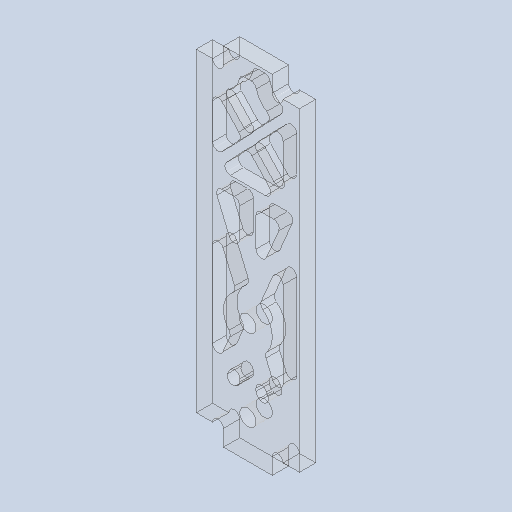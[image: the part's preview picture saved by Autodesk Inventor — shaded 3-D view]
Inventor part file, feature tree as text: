
AUTODESK INVENTOR PART (.ipt)
format: ipt  version: 2023 (Build 270158030, 158C)  size: 849,408 bytes
history: native  units: mm
features: sketch x19, other x17, extrude x16, fillet x3, projected_geometry x2, hole x1
ambient origin geometry x8: Origin, YZ Plane, XZ Plane, XY Plane, X Axis, Y Axis, Z Axis, Center Point
bodies: Body1 (feature_tree)
feature tree (58):
  other  "ソリッド1"
  extrude  "押し出し1"  Depth=40.0mm
  extrude  "押し出し2"  Depth=6.0mm
  extrude  "押し出し3"  Depth=6.0mm
  hole  "穴1"  [1 undecoded]
  extrude  "押し出し4"  Depth=9.0mm
  sketch  "スケッチ6"
  extrude  "押し出し5"  Depth=19.0mm
  sketch  "スケッチ8"
  extrude  "押し出し6"  Depth=9.0mm
  extrude  "押し出し7"  Depth=5.0mm
  extrude  "押し出し8"  Depth=3.0mm
  fillet  "フィレット1"  Radius=9.0mm
  sketch  "スケッチ9"
  sketch  "スケッチ10"
  extrude  "押し出し9"  Depth=3.0mm
  extrude  "押し出し10"  Depth=3.0mm TaperAngle=0.0deg
  extrude  "押し出し11"  Depth=2.0mm
  extrude  "押し出し12"  Depth=2.0mm
  extrude  "押し出し13"  Depth=2.0mm
  fillet  "フィレット2"  Radius=2.0mm
  sketch  "スケッチ16"
  extrude  "押し出し14"  Depth=10.0mm TaperAngle=0.0deg
  extrude  "押し出し15"  Depth=6.0mm
  extrude  "押し出し16"  Depth=6.0mm
  fillet  "フィレット3"  Radius=15.0mm
  sketch  "スケッチ1"
  sketch  "スケッチ2"
  sketch  "スケッチ3"
  sketch  "スケッチ4"
  sketch  "スケッチ5"
  sketch  "スケッチ7"
  projected_geometry  "投影ループ1"
  sketch  "スケッチ11"
  sketch  "スケッチ12"
  sketch  "スケッチ13"
  sketch  "スケッチ14"
  sketch  "スケッチ15"
  sketch  "スケッチ17"
  sketch  "スケッチ18"
  projected_geometry  "投影ループ2"
  sketch  "スケッチ19"
  other  "断面エッジを投影1"
  other  "断面エッジを投影2"
  other  "断面エッジを投影3"
  other  "断面エッジを投影4"
  other  "断面エッジを投影5"
  other  "断面エッジを投影6"
  other  "断面エッジを投影7"
  other  "断面エッジを投影8"
  other  "断面エッジを投影9"
  other  "断面エッジを投影10"
  other  "断面エッジを投影11"
  other  "断面エッジを投影12"
  other  "断面エッジを投影13"
  other  "断面エッジを投影14"
  other  "断面エッジを投影15"
  other  "断面エッジを投影16"
note: 1 required parameter value undecoded (feature->parameter linkage not recoverable at this tier; creation-order binding heuristic only, values carry confidence <= 0.55)
